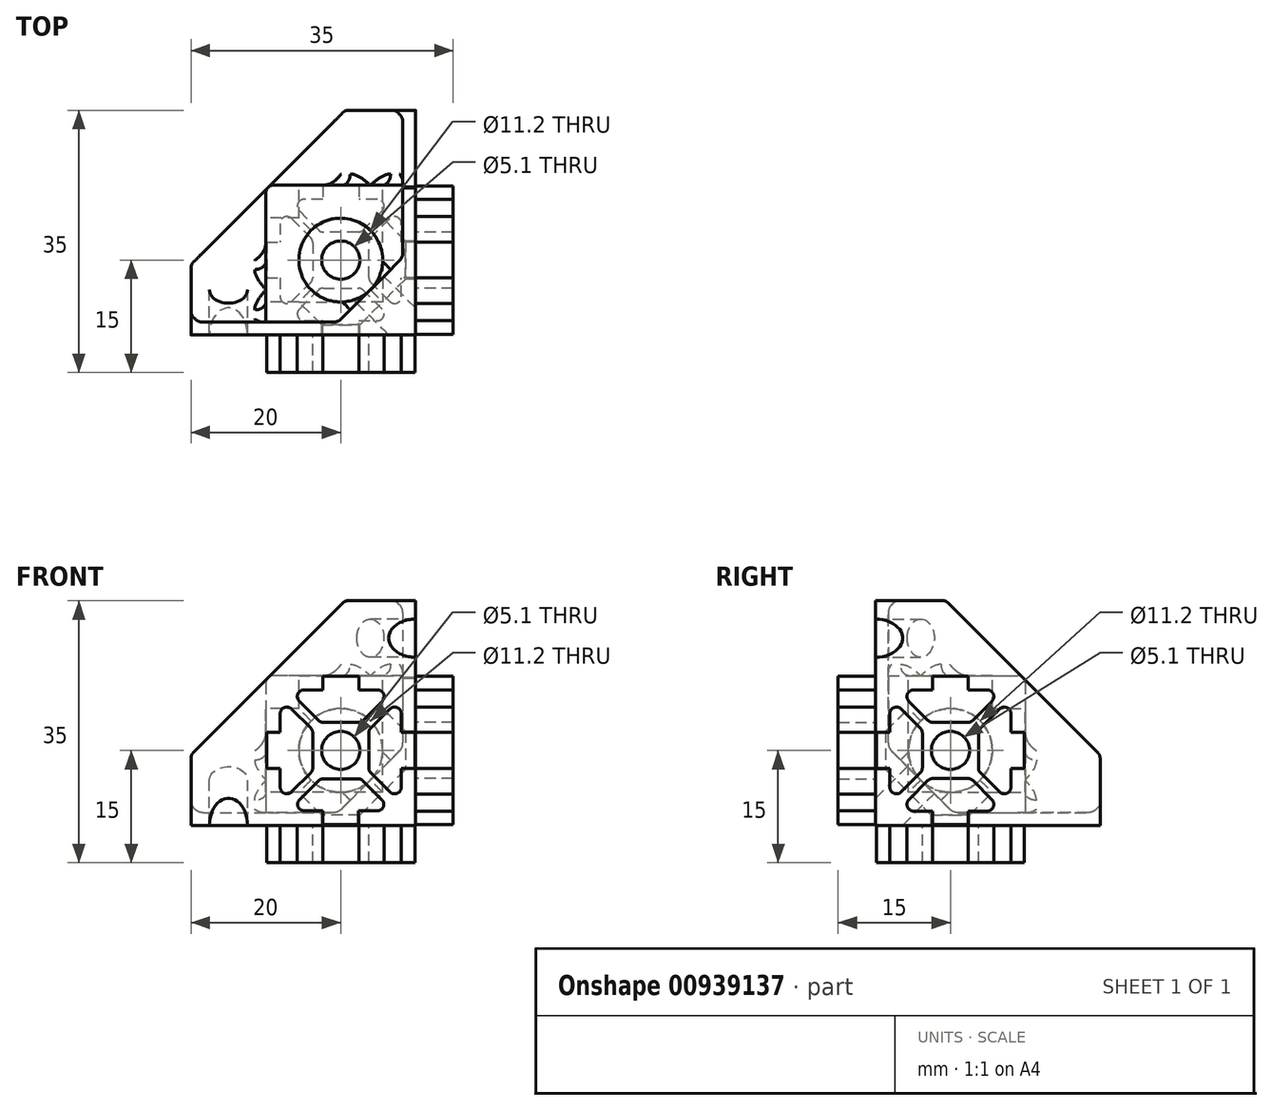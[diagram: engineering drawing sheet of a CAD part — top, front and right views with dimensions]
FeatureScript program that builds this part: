
annotation { "Feature Type Name" : "Feature", "Feature Type Description" : "" }
export const myFeature = defineFeature(function(context is Context, id is Id, definition is map)
    precondition{}
    {
        {
            var Q0;
            Q0=qCreatedBy(makeId("Top.planeOp"),FACE);
            var sketch = newSketch(context, id + "F0", { "sketchPlane" : qUnion([Q0]) });
            skLineSegment(sketch, "E0.bottom", {"start": v(0, 0) * mm, "end": v(-20, 0) * mm});
            skLineSegment(sketch, "E0.top", {"start": v(0, 20) * mm, "end": v(-20, 20) * mm});
            skLineSegment(sketch, "E0.left", {"start": v(0, 0) * mm, "end": v(0, 20) * mm});
            skLineSegment(sketch, "E0.right", {"start": v(-20, 0) * mm, "end": v(-20, 20) * mm});
            skSolve(sketch);
        }
        {
            var Q0;
            Q0 = qSketchRegion(id + "F0", true);
            extrude(context, id + "F1", {"entities" : qUnion([Q0]), "depth" : 20 * mm, "offsetDistance" : 25 * mm});
        }
        {
            var Q0;
            Q0=makeQuery(id+"FwfA9fW3TVrLifJ_1.boolean.opBoolean","SPLIT",EDGE,{"derivedFrom":makeQuery(id+"F1.opExtrude","CAP_EDGE",EDGE,{"disambiguationData":[OSD([sQuery(id+"F0.wireOp",EDGE,"E0.right")])],"isStart":false})});
            var Q1;
            Q1=makeQuery(id+"FhSoDMzTukZfK2q_1.boolean.opBoolean","SPLIT",EDGE,{"derivedFrom":makeQuery(id+"F1.opExtrude","SWEPT_EDGE",EDGE,{"disambiguationData":[OSD([sQuery(id+"F0.wireOp",EDGE,"E0.top"),sQuery(id+"F0.wireOp",EDGE,"E0.right")])]})});
            var Q2;
            Q2=makeQuery(id+"F1.opExtrude","CAP_EDGE",EDGE,{"disambiguationData":[OSD([sQuery(id+"F0.wireOp",EDGE,"E0.top")])],"isStart":false});
            fillet(context, id + "F2", {"entities" : qUnion([Q0, Q1, Q2]), "radius" : 1 * mm, "tangentPropagation" : true});
        }
        {
            var Q0;
            Q0=qCreatedBy(makeId("Front.planeOp"),FACE);
            cPlane(context, id + "F3", {"entities" : qUnion([Q0]), "cplaneType" : CPlaneType.OFFSET, "offset" : 10 * mm, "oppositeDirection" : true, "width" : 150 * mm, "height" : 150 * mm});
        }
        {
            var Q0;
            Q0=qCreatedBy(id+"F3.planeOp",FACE);
            var sketch = newSketch(context, id + "F4", { "sketchPlane" : qUnion([Q0]) });
            skLineSegment(sketch, "E1", {"start": v(0, 10) * mm, "end": v(-20, 10) * mm});
            skLineSegment(sketch, "E2", {"start": v(0, 7.45) * mm, "end": v(-1.35, 7.45) * mm});
            skLineSegment(sketch, "E3", {"start": v(-4.4, 4.4) * mm, "end": v(-20, 4.4) * mm});
            skLineSegment(sketch, "E4", {"start": v(-1.35, 7.45) * mm, "end": v(-4.4, 4.4) * mm});
            skLineSegment(sketch, "E5", {"start": v(-20, 10) * mm, "end": v(-20, 4.4) * mm});
            skLineSegment(sketch, "E6", {"start": v(0, 10) * mm, "end": v(0, 7.45) * mm});
            skSolve(sketch);
        }
        {
            var Q0;
            Q0 = qSketchRegion(id + "F4", true);
            var Q1;
            Q1=sQuery(id+"F4.wireOp",EDGE,"E1");
            revolve(context, id + "F5", {"operationType" : NewBodyOperationType.REMOVE, "surfaceOperationType" : NewSurfaceOperationType.NEW, "entities" : qUnion([Q0]), "axis" : qUnion([Q1]), "revolveType" : RevolveType.FULL, "oppositeDirection" : true});
        }
        {
            var Q0;
            Q0=qCreatedBy(id+"F3.planeOp",FACE);
            var sketch = newSketch(context, id + "F6", { "sketchPlane" : qUnion([Q0]) });
            skLineSegment(sketch, "E7", {"start": v(-15.6, 20) * mm, "end": v(-10, 20) * mm});
            skLineSegment(sketch, "E8", {"start": v(-10, 0) * mm, "end": v(-12.55, 0) * mm});
            skLineSegment(sketch, "E9", {"start": v(-10, 0) * mm, "end": v(-10, 20) * mm});
            skLineSegment(sketch, "E10", {"start": v(-12.55, 0) * mm, "end": v(-12.55, 1.35) * mm});
            skLineSegment(sketch, "E11", {"start": v(-15.6, 4.4) * mm, "end": v(-15.6, 20) * mm});
            skLineSegment(sketch, "E12", {"start": v(-12.55, 1.35) * mm, "end": v(-15.6, 4.4) * mm});
            skSolve(sketch);
        }
        {
            var Q0;
            Q0 = qSketchRegion(id + "F6", true);
            var Q1;
            Q1=sQuery(id+"F6.wireOp",EDGE,"E9");
            revolve(context, id + "F7", {"operationType" : NewBodyOperationType.REMOVE, "surfaceOperationType" : NewSurfaceOperationType.NEW, "entities" : qUnion([Q0]), "axis" : qUnion([Q1]), "revolveType" : RevolveType.FULL, "oppositeDirection" : true});
        }
        {
            var Q0;
            Q0=qCreatedBy(makeId("Right.planeOp"),FACE);
            cPlane(context, id + "F8", {"entities" : qUnion([Q0]), "cplaneType" : CPlaneType.OFFSET, "offset" : 10 * mm, "oppositeDirection" : true, "width" : 150 * mm, "height" : 150 * mm});
        }
        {
            var Q0;
            Q0=qCreatedBy(id+"F8.planeOp",FACE);
            var sketch = newSketch(context, id + "F9", { "sketchPlane" : qUnion([Q0]) });
            skLineSegment(sketch, "E13", {"start": v(20, 15.6) * mm, "end": v(20, 10) * mm});
            skLineSegment(sketch, "E14", {"start": v(0, 10) * mm, "end": v(0, 12.55) * mm});
            skLineSegment(sketch, "E15", {"start": v(0, 10) * mm, "end": v(20, 10) * mm});
            skLineSegment(sketch, "E16", {"start": v(0, 12.55) * mm, "end": v(1.35, 12.55) * mm});
            skLineSegment(sketch, "E17", {"start": v(4.4, 15.6) * mm, "end": v(20, 15.6) * mm});
            skLineSegment(sketch, "E18", {"start": v(1.35, 12.55) * mm, "end": v(4.4, 15.6) * mm});
            skSolve(sketch);
        }
        {
            var Q0;
            Q0 = qSketchRegion(id + "F9", true);
            var Q1;
            Q1=sQuery(id+"F9.wireOp",EDGE,"E15");
            revolve(context, id + "F10", {"operationType" : NewBodyOperationType.REMOVE, "surfaceOperationType" : NewSurfaceOperationType.NEW, "entities" : qUnion([Q0]), "axis" : qUnion([Q1]), "revolveType" : RevolveType.FULL, "oppositeDirection" : true});
        }
        {
            var Q0;
            Q0=makeQuery(id+"F1.opExtrude","SWEPT_FACE",FACE,{"disambiguationData":[OSD([sQuery(id+"F0.wireOp",EDGE,"E0.bottom")])]});
            var sketch = newSketch(context, id + "F11", { "sketchPlane" : qUnion([Q0]) });
            skLineSegment(sketch, "E19", {"start": v(-1.8, 12.5) * mm, "end": v(0, 12.5) * mm});
            skLineSegment(sketch, "E20", {"start": v(-20, 12.5) * mm, "end": v(-18.2, 12.5) * mm});
            skLineSegment(sketch, "E21", {"start": v(-1.8, 7.5) * mm, "end": v(0, 7.5) * mm});
            skLineSegment(sketch, "E22", {"start": v(-20, 7.5) * mm, "end": v(-18.2, 7.5) * mm});
            skLineSegment(sketch, "E23", {"start": v(-12.5, 1.8) * mm, "end": v(-12.5, 0) * mm});
            skLineSegment(sketch, "E24", {"start": v(-12.5, 20) * mm, "end": v(-12.5, 18.2) * mm});
            skLineSegment(sketch, "E25", {"start": v(-7.54, 1.76) * mm, "end": v(-7.54, 0) * mm});
            skLineSegment(sketch, "E26", {"start": v(-7.5, 20) * mm, "end": v(-7.5, 18.2) * mm});
            skLineSegment(sketch, "E27", {"start": v(-7.5, 1.84) * mm, "end": v(-5.1, 1.84) * mm});
            skLineSegment(sketch, "E28", {"start": v(-1.8, 5.1) * mm, "end": v(-1.8, 7.5) * mm});
            skLineSegment(sketch, "E29", {"start": v(-1.8, 12.5) * mm, "end": v(-1.8, 14.9) * mm});
            skLineSegment(sketch, "E30", {"start": v(-7.5, 18.2) * mm, "end": v(-5.1, 18.2) * mm});
            skLineSegment(sketch, "E31", {"start": v(-14.9, 18.2) * mm, "end": v(-12.5, 18.2) * mm});
            skLineSegment(sketch, "E32", {"start": v(-18.2, 14.9) * mm, "end": v(-18.2, 12.5) * mm});
            skLineSegment(sketch, "E33", {"start": v(-18.2, 7.5) * mm, "end": v(-18.2, 5.1) * mm});
            skLineSegment(sketch, "E34", {"start": v(-14.9, 1.84) * mm, "end": v(-12.5, 1.84) * mm});
            skLineSegment(sketch, "E35", {"start": v(-6.06, 6.94) * mm, "end": v(-3.5, 4.4) * mm});
            skLineSegment(sketch, "E36", {"start": v(-15.6, 16.5) * mm, "end": v(-13.06, 13.94) * mm});
            skLineSegment(sketch, "E37", {"start": v(-6.97, 6.03) * mm, "end": v(-4.42, 3.48) * mm});
            skLineSegment(sketch, "E38", {"start": v(-16.5, 15.6) * mm, "end": v(-13.94, 13.06) * mm});
            skLineSegment(sketch, "E39", {"start": v(-13.94, 6.94) * mm, "end": v(-16.5, 4.4) * mm});
            skLineSegment(sketch, "E40", {"start": v(-4.4, 16.5) * mm, "end": v(-6.94, 13.94) * mm});
            skLineSegment(sketch, "E41", {"start": v(-6.06, 13.06) * mm, "end": v(-3.5, 15.6) * mm});
            skLineSegment(sketch, "E42", {"start": v(-15.58, 3.48) * mm, "end": v(-13.03, 6.03) * mm});
            skLineSegment(sketch, "E43", {"start": v(-13.65, 12.35) * mm, "end": v(-13.65, 7.65) * mm});
            skLineSegment(sketch, "E44", {"start": v(-6.35, 7.65) * mm, "end": v(-6.35, 12.35) * mm});
            skArc(sketch, "E45", {"start": v(-6.35, 7.65) * mm, "mid": v(-6.27, 7.27) * mm, "end": v(-6.06, 6.94) * mm});
            skArc(sketch, "E46", {"start": v(-6.06, 13.06) * mm, "mid": v(-6.27, 12.73) * mm, "end": v(-6.35, 12.35) * mm});
            skArc(sketch, "E47", {"start": v(-13.94, 6.94) * mm, "mid": v(-13.73, 7.27) * mm, "end": v(-13.65, 7.65) * mm});
            skArc(sketch, "E48", {"start": v(-13.65, 12.35) * mm, "mid": v(-13.73, 12.73) * mm, "end": v(-13.94, 13.06) * mm});
            skLineSegment(sketch, "E49", {"start": v(-12.35, 13.65) * mm, "end": v(-7.65, 13.65) * mm});
            skLineSegment(sketch, "E50", {"start": v(-12.35, 6.31) * mm, "end": v(-7.65, 6.31) * mm});
            skArc(sketch, "E51", {"start": v(-6.97, 6.03) * mm, "mid": v(-7.28, 6.24) * mm, "end": v(-7.65, 6.31) * mm});
            skArc(sketch, "E52", {"start": v(-7.65, 13.65) * mm, "mid": v(-7.27, 13.73) * mm, "end": v(-6.94, 13.94) * mm});
            skArc(sketch, "E53", {"start": v(-12.35, 6.31) * mm, "mid": v(-12.72, 6.24) * mm, "end": v(-13.03, 6.03) * mm});
            skArc(sketch, "E54", {"start": v(-13.06, 13.94) * mm, "mid": v(-12.73, 13.73) * mm, "end": v(-12.35, 13.65) * mm});
            skArc(sketch, "E55", {"start": v(-16.5, 15.6) * mm, "mid": v(-17.58, 15.82) * mm, "end": v(-18.2, 14.9) * mm});
            skArc(sketch, "E56", {"start": v(-14.9, 18.2) * mm, "mid": v(-15.82, 17.58) * mm, "end": v(-15.6, 16.5) * mm});
            skArc(sketch, "E57", {"start": v(-4.4, 16.5) * mm, "mid": v(-4.18, 17.58) * mm, "end": v(-5.1, 18.2) * mm});
            skArc(sketch, "E58", {"start": v(-1.8, 14.9) * mm, "mid": v(-2.42, 15.82) * mm, "end": v(-3.5, 15.6) * mm});
            skArc(sketch, "E59", {"start": v(-3.5, 4.4) * mm, "mid": v(-2.42, 4.18) * mm, "end": v(-1.8, 5.1) * mm});
            skArc(sketch, "E60", {"start": v(-5.1, 1.84) * mm, "mid": v(-4.21, 2.43) * mm, "end": v(-4.42, 3.48) * mm});
            skArc(sketch, "E61", {"start": v(-15.58, 3.48) * mm, "mid": v(-15.79, 2.43) * mm, "end": v(-14.9, 1.84) * mm});
            skArc(sketch, "E62", {"start": v(-18.2, 5.1) * mm, "mid": v(-17.58, 4.18) * mm, "end": v(-16.5, 4.4) * mm});
            skLineSegment(sketch, "E63", {"start": v(-12.5, 20) * mm, "end": v(-7.5, 20) * mm});
            skLineSegment(sketch, "E64", {"start": v(-20, 12.5) * mm, "end": v(-20, 7.5) * mm});
            skLineSegment(sketch, "E65", {"start": v(-12.5, 0) * mm, "end": v(-7.54, 0) * mm});
            skLineSegment(sketch, "E66", {"start": v(0, 12.5) * mm, "end": v(0, 7.5) * mm});
            skLineSegment(sketch, "E67.0", {"start": v(-12.4, 19.9) * mm, "end": v(-7.6, 19.9) * mm});
            skArc(sketch, "E67.1", {"start": v(-12.99, 14.01) * mm, "mid": v(-12.7, 13.82) * mm, "end": v(-12.35, 13.75) * mm});
            skLineSegment(sketch, "E67.2", {"start": v(-15.54, 16.56) * mm, "end": v(-12.99, 14.01) * mm});
            skArc(sketch, "E67.3", {"start": v(-14.9, 18.1) * mm, "mid": v(-15.73, 17.54) * mm, "end": v(-15.54, 16.56) * mm});
            skLineSegment(sketch, "E67.4", {"start": v(-14.9, 18.1) * mm, "end": v(-12.4, 18.1) * mm});
            skLineSegment(sketch, "E67.5", {"start": v(-12.35, 13.75) * mm, "end": v(-7.65, 13.75) * mm});
            skLineSegment(sketch, "E67.6", {"start": v(-12.4, 19.9) * mm, "end": v(-12.4, 18.1) * mm});
            skArc(sketch, "E67.7", {"start": v(-7.65, 13.75) * mm, "mid": v(-7.3, 13.82) * mm, "end": v(-7.01, 14.01) * mm});
            skLineSegment(sketch, "E67.8", {"start": v(-4.46, 16.56) * mm, "end": v(-7.01, 14.01) * mm});
            skArc(sketch, "E67.9", {"start": v(-4.46, 16.56) * mm, "mid": v(-4.27, 17.54) * mm, "end": v(-5.1, 18.1) * mm});
            skLineSegment(sketch, "E67.10", {"start": v(-7.6, 18.1) * mm, "end": v(-5.1, 18.1) * mm});
            skLineSegment(sketch, "E67.11", {"start": v(-7.6, 19.9) * mm, "end": v(-7.6, 18.1) * mm});
            skArc(sketch, "E68.0", {"start": v(-13.75, 12.35) * mm, "mid": v(-13.82, 12.7) * mm, "end": v(-14.01, 12.99) * mm});
            skLineSegment(sketch, "E68.1", {"start": v(-18.1, 7.6) * mm, "end": v(-18.1, 5.1) * mm});
            skArc(sketch, "E68.2", {"start": v(-18.1, 5.1) * mm, "mid": v(-17.54, 4.27) * mm, "end": v(-16.56, 4.46) * mm});
            skLineSegment(sketch, "E68.3", {"start": v(-14.01, 7.01) * mm, "end": v(-16.56, 4.46) * mm});
            skArc(sketch, "E68.4", {"start": v(-14.01, 7.01) * mm, "mid": v(-13.82, 7.3) * mm, "end": v(-13.75, 7.65) * mm});
            skLineSegment(sketch, "E68.5", {"start": v(-19.9, 7.6) * mm, "end": v(-18.1, 7.6) * mm});
            skLineSegment(sketch, "E68.6", {"start": v(-13.75, 12.35) * mm, "end": v(-13.75, 7.65) * mm});
            skLineSegment(sketch, "E68.7", {"start": v(-19.9, 12.4) * mm, "end": v(-19.9, 7.6) * mm});
            skLineSegment(sketch, "E68.8", {"start": v(-19.9, 12.4) * mm, "end": v(-18.1, 12.4) * mm});
            skLineSegment(sketch, "E68.9", {"start": v(-18.1, 14.9) * mm, "end": v(-18.1, 12.4) * mm});
            skArc(sketch, "E68.10", {"start": v(-16.56, 15.54) * mm, "mid": v(-17.54, 15.73) * mm, "end": v(-18.1, 14.9) * mm});
            skLineSegment(sketch, "E68.11", {"start": v(-16.56, 15.54) * mm, "end": v(-14.01, 12.99) * mm});
            skArc(sketch, "E69.0", {"start": v(-12.35, 6.21) * mm, "mid": v(-12.68, 6.14) * mm, "end": v(-12.96, 5.96) * mm});
            skLineSegment(sketch, "E69.1", {"start": v(-7.64, 1.94) * mm, "end": v(-5.1, 1.94) * mm});
            skArc(sketch, "E69.2", {"start": v(-5.1, 1.94) * mm, "mid": v(-4.3, 2.47) * mm, "end": v(-4.5, 3.4) * mm});
            skLineSegment(sketch, "E69.3", {"start": v(-7.04, 5.96) * mm, "end": v(-4.5, 3.4) * mm});
            skArc(sketch, "E69.4", {"start": v(-7.04, 5.96) * mm, "mid": v(-7.32, 6.14) * mm, "end": v(-7.65, 6.21) * mm});
            skLineSegment(sketch, "E69.5", {"start": v(-7.64, 1.94) * mm, "end": v(-7.64, 0.1) * mm});
            skLineSegment(sketch, "E69.6", {"start": v(-12.35, 6.21) * mm, "end": v(-7.65, 6.21) * mm});
            skLineSegment(sketch, "E69.7", {"start": v(-12.4, 0.1) * mm, "end": v(-7.64, 0.1) * mm});
            skLineSegment(sketch, "E69.8", {"start": v(-12.4, 1.94) * mm, "end": v(-12.4, 0.1) * mm});
            skLineSegment(sketch, "E69.9", {"start": v(-14.9, 1.94) * mm, "end": v(-12.4, 1.94) * mm});
            skArc(sketch, "E69.10", {"start": v(-15.5, 3.4) * mm, "mid": v(-15.7, 2.47) * mm, "end": v(-14.9, 1.94) * mm});
            skLineSegment(sketch, "E69.11", {"start": v(-15.5, 3.4) * mm, "end": v(-12.96, 5.96) * mm});
            skArc(sketch, "E70.0", {"start": v(-6.25, 7.65) * mm, "mid": v(-6.18, 7.3) * mm, "end": v(-5.99, 7.01) * mm});
            skLineSegment(sketch, "E70.1", {"start": v(-1.9, 12.4) * mm, "end": v(-1.9, 14.9) * mm});
            skArc(sketch, "E70.2", {"start": v(-1.9, 14.9) * mm, "mid": v(-2.46, 15.73) * mm, "end": v(-3.44, 15.54) * mm});
            skLineSegment(sketch, "E70.3", {"start": v(-5.99, 12.99) * mm, "end": v(-3.44, 15.54) * mm});
            skArc(sketch, "E70.4", {"start": v(-5.99, 12.99) * mm, "mid": v(-6.18, 12.7) * mm, "end": v(-6.25, 12.35) * mm});
            skLineSegment(sketch, "E70.5", {"start": v(-1.9, 12.4) * mm, "end": v(-0.1, 12.4) * mm});
            skLineSegment(sketch, "E70.6", {"start": v(-6.25, 7.65) * mm, "end": v(-6.25, 12.35) * mm});
            skLineSegment(sketch, "E70.7", {"start": v(-0.1, 12.4) * mm, "end": v(-0.1, 7.6) * mm});
            skLineSegment(sketch, "E70.8", {"start": v(-1.9, 7.6) * mm, "end": v(-0.1, 7.6) * mm});
            skLineSegment(sketch, "E70.9", {"start": v(-1.9, 5.1) * mm, "end": v(-1.9, 7.6) * mm});
            skArc(sketch, "E70.10", {"start": v(-3.44, 4.46) * mm, "mid": v(-2.46, 4.27) * mm, "end": v(-1.9, 5.1) * mm});
            skLineSegment(sketch, "E70.11", {"start": v(-5.99, 7.01) * mm, "end": v(-3.44, 4.46) * mm});
            skSolve(sketch);
        }
        {
            var Q0;
            Q0=makeQuery(id+"F11.imprint","IMPRINT",FACE,{"disambiguationData":[TD([[makeQuery(id+"F11.imprint","IMPRINT",EDGE,{"derivedFrom":sQuery(id+"F11.wireOp",EDGE,"E67.0")}),-1.0]])]});
            var Q1;
            Q1=makeQuery(id+"F11.imprint","IMPRINT",FACE,{"disambiguationData":[TD([[makeQuery(id+"F11.imprint","IMPRINT",EDGE,{"derivedFrom":sQuery(id+"F11.wireOp",EDGE,"E68.0")}),1.0]])]});
            var Q2;
            Q2=makeQuery(id+"F11.imprint","IMPRINT",FACE,{"disambiguationData":[TD([[makeQuery(id+"F11.imprint","IMPRINT",EDGE,{"derivedFrom":sQuery(id+"F11.wireOp",EDGE,"E70.0")}),1.0]])]});
            var Q3;
            Q3=makeQuery(id+"F11.imprint","IMPRINT",FACE,{"disambiguationData":[TD([[makeQuery(id+"F11.imprint","IMPRINT",EDGE,{"derivedFrom":sQuery(id+"F11.wireOp",EDGE,"E69.0")}),1.0]])]});
            extrude(context, id + "F12", {"entities" : qUnion([Q0, Q1, Q2, Q3]), "operationType" : NewBodyOperationType.ADD, "depth" : 5 * mm, "offsetDistance" : 25 * mm});
        }
        {
            var Q0;
            Q0=makeQuery(id+"F1.opExtrude","SWEPT_FACE",FACE,{"disambiguationData":[OSD([sQuery(id+"F0.wireOp",EDGE,"E0.left")])]});
            var sketch = newSketch(context, id + "F13", { "sketchPlane" : qUnion([Q0]) });
            skLineSegment(sketch, "E71", {"start": v(7.5, 20) * mm, "end": v(7.5, 18.2) * mm});
            skLineSegment(sketch, "E72", {"start": v(12.5, 20) * mm, "end": v(12.5, 18.2) * mm});
            skLineSegment(sketch, "E73", {"start": v(12.5, 18.2) * mm, "end": v(14.9, 18.2) * mm});
            skLineSegment(sketch, "E74", {"start": v(5.1, 18.2) * mm, "end": v(7.5, 18.2) * mm});
            skLineSegment(sketch, "E75", {"start": v(4.4, 16.5) * mm, "end": v(6.94, 13.94) * mm});
            skLineSegment(sketch, "E76", {"start": v(15.6, 16.5) * mm, "end": v(13.06, 13.94) * mm});
            skLineSegment(sketch, "E77", {"start": v(7.65, 13.65) * mm, "end": v(12.35, 13.65) * mm});
            skArc(sketch, "E78", {"start": v(12.35, 13.65) * mm, "mid": v(12.73, 13.73) * mm, "end": v(13.06, 13.94) * mm});
            skArc(sketch, "E79", {"start": v(6.94, 13.94) * mm, "mid": v(7.27, 13.73) * mm, "end": v(7.65, 13.65) * mm});
            skArc(sketch, "E80", {"start": v(5.1, 18.2) * mm, "mid": v(4.18, 17.58) * mm, "end": v(4.4, 16.5) * mm});
            skArc(sketch, "E81", {"start": v(15.6, 16.5) * mm, "mid": v(15.82, 17.58) * mm, "end": v(14.9, 18.2) * mm});
            skLineSegment(sketch, "E82", {"start": v(7.5, 20) * mm, "end": v(12.5, 20) * mm});
            skPoint(sketch, "E83", {"position": v(10, 10) * mm});
            skArc(sketch, "E84.0", {"start": v(7.01, 14.01) * mm, "mid": v(7.3, 13.82) * mm, "end": v(7.65, 13.75) * mm});
            skLineSegment(sketch, "E84.1", {"start": v(12.4, 18.1) * mm, "end": v(14.9, 18.1) * mm});
            skArc(sketch, "E84.2", {"start": v(15.54, 16.56) * mm, "mid": v(15.73, 17.54) * mm, "end": v(14.9, 18.1) * mm});
            skLineSegment(sketch, "E84.3", {"start": v(15.54, 16.56) * mm, "end": v(12.99, 14.01) * mm});
            skArc(sketch, "E84.4", {"start": v(12.35, 13.75) * mm, "mid": v(12.7, 13.82) * mm, "end": v(12.99, 14.01) * mm});
            skLineSegment(sketch, "E84.5", {"start": v(12.4, 19.9) * mm, "end": v(12.4, 18.1) * mm});
            skLineSegment(sketch, "E84.6", {"start": v(7.65, 13.75) * mm, "end": v(12.35, 13.75) * mm});
            skLineSegment(sketch, "E84.7", {"start": v(7.6, 19.9) * mm, "end": v(12.4, 19.9) * mm});
            skLineSegment(sketch, "E84.8", {"start": v(7.6, 19.9) * mm, "end": v(7.6, 18.1) * mm});
            skLineSegment(sketch, "E84.9", {"start": v(5.1, 18.1) * mm, "end": v(7.6, 18.1) * mm});
            skArc(sketch, "E84.10", {"start": v(5.1, 18.1) * mm, "mid": v(4.27, 17.54) * mm, "end": v(4.46, 16.56) * mm});
            skLineSegment(sketch, "E84.11", {"start": v(4.46, 16.56) * mm, "end": v(7.01, 14.01) * mm});
            skLineSegment(sketch, "E85.1.0", {"start": v(0.1, 7.6) * mm, "end": v(1.9, 7.6) * mm});
            skLineSegment(sketch, "E85.1.1", {"start": v(1.9, 5.1) * mm, "end": v(1.9, 7.6) * mm});
            skArc(sketch, "E85.1.2", {"start": v(1.9, 5.1) * mm, "mid": v(2.46, 4.27) * mm, "end": v(3.44, 4.46) * mm});
            skLineSegment(sketch, "E85.1.3", {"start": v(3.44, 4.46) * mm, "end": v(5.99, 7.01) * mm});
            skArc(sketch, "E85.1.4", {"start": v(5.99, 7.01) * mm, "mid": v(6.18, 7.3) * mm, "end": v(6.25, 7.65) * mm});
            skLineSegment(sketch, "E85.1.5", {"start": v(6.25, 7.65) * mm, "end": v(6.25, 12.35) * mm});
            skArc(sketch, "E85.1.6", {"start": v(6.25, 12.35) * mm, "mid": v(6.18, 12.7) * mm, "end": v(5.99, 12.99) * mm});
            skLineSegment(sketch, "E85.1.7", {"start": v(3.44, 15.54) * mm, "end": v(5.99, 12.99) * mm});
            skArc(sketch, "E85.1.8", {"start": v(3.44, 15.54) * mm, "mid": v(2.46, 15.73) * mm, "end": v(1.9, 14.9) * mm});
            skLineSegment(sketch, "E85.1.9", {"start": v(1.9, 12.4) * mm, "end": v(1.9, 14.9) * mm});
            skLineSegment(sketch, "E85.1.10", {"start": v(0.1, 12.4) * mm, "end": v(1.9, 12.4) * mm});
            skLineSegment(sketch, "E85.1.11", {"start": v(0.1, 7.6) * mm, "end": v(0.1, 12.4) * mm});
            skLineSegment(sketch, "E85.2.0", {"start": v(12.4, 0.1) * mm, "end": v(12.4, 1.9) * mm});
            skLineSegment(sketch, "E85.2.1", {"start": v(14.9, 1.9) * mm, "end": v(12.4, 1.9) * mm});
            skArc(sketch, "E85.2.2", {"start": v(14.9, 1.9) * mm, "mid": v(15.73, 2.46) * mm, "end": v(15.54, 3.44) * mm});
            skLineSegment(sketch, "E85.2.3", {"start": v(15.54, 3.44) * mm, "end": v(12.99, 5.99) * mm});
            skArc(sketch, "E85.2.4", {"start": v(12.99, 5.99) * mm, "mid": v(12.7, 6.18) * mm, "end": v(12.35, 6.25) * mm});
            skLineSegment(sketch, "E85.2.5", {"start": v(12.35, 6.25) * mm, "end": v(7.65, 6.25) * mm});
            skArc(sketch, "E85.2.6", {"start": v(7.65, 6.25) * mm, "mid": v(7.3, 6.18) * mm, "end": v(7.01, 5.99) * mm});
            skLineSegment(sketch, "E85.2.7", {"start": v(4.46, 3.44) * mm, "end": v(7.01, 5.99) * mm});
            skArc(sketch, "E85.2.8", {"start": v(4.46, 3.44) * mm, "mid": v(4.27, 2.46) * mm, "end": v(5.1, 1.9) * mm});
            skLineSegment(sketch, "E85.2.9", {"start": v(7.6, 1.9) * mm, "end": v(5.1, 1.9) * mm});
            skLineSegment(sketch, "E85.2.10", {"start": v(7.6, 0.1) * mm, "end": v(7.6, 1.9) * mm});
            skLineSegment(sketch, "E85.2.11", {"start": v(12.4, 0.1) * mm, "end": v(7.6, 0.1) * mm});
            skLineSegment(sketch, "E85.3.0", {"start": v(19.9, 12.4) * mm, "end": v(18.1, 12.4) * mm});
            skLineSegment(sketch, "E85.3.1", {"start": v(18.1, 14.9) * mm, "end": v(18.1, 12.4) * mm});
            skArc(sketch, "E85.3.2", {"start": v(18.1, 14.9) * mm, "mid": v(17.54, 15.73) * mm, "end": v(16.56, 15.54) * mm});
            skLineSegment(sketch, "E85.3.3", {"start": v(16.56, 15.54) * mm, "end": v(14.01, 12.99) * mm});
            skArc(sketch, "E85.3.4", {"start": v(14.01, 12.99) * mm, "mid": v(13.82, 12.7) * mm, "end": v(13.75, 12.35) * mm});
            skLineSegment(sketch, "E85.3.5", {"start": v(13.75, 12.35) * mm, "end": v(13.75, 7.65) * mm});
            skArc(sketch, "E85.3.6", {"start": v(13.75, 7.65) * mm, "mid": v(13.82, 7.3) * mm, "end": v(14.01, 7.01) * mm});
            skLineSegment(sketch, "E85.3.7", {"start": v(16.56, 4.46) * mm, "end": v(14.01, 7.01) * mm});
            skArc(sketch, "E85.3.8", {"start": v(16.56, 4.46) * mm, "mid": v(17.54, 4.27) * mm, "end": v(18.1, 5.1) * mm});
            skLineSegment(sketch, "E85.3.9", {"start": v(18.1, 7.6) * mm, "end": v(18.1, 5.1) * mm});
            skLineSegment(sketch, "E85.3.10", {"start": v(19.9, 7.6) * mm, "end": v(18.1, 7.6) * mm});
            skLineSegment(sketch, "E85.3.11", {"start": v(19.9, 12.4) * mm, "end": v(19.9, 7.6) * mm});
            skSolve(sketch);
        }
        {
            var Q0;
            Q0=makeQuery(id+"F13.imprint","IMPRINT",FACE,{"disambiguationData":[TD([[makeQuery(id+"F13.imprint","IMPRINT",EDGE,{"derivedFrom":sQuery(id+"F13.wireOp",EDGE,"E84.0")}),1.0]])]});
            var Q1;
            Q1=makeQuery(id+"F13.imprint","IMPRINT",FACE,{"disambiguationData":[TD([[makeQuery(id+"F13.imprint","IMPRINT",EDGE,{"derivedFrom":sQuery(id+"F13.wireOp",EDGE,"E85.3.0")}),1.0]])]});
            var Q2;
            Q2=makeQuery(id+"F13.imprint","IMPRINT",FACE,{"disambiguationData":[TD([[makeQuery(id+"F13.imprint","IMPRINT",EDGE,{"derivedFrom":sQuery(id+"F13.wireOp",EDGE,"E85.2.0")}),1.0]])]});
            var Q3;
            Q3=makeQuery(id+"F13.imprint","IMPRINT",FACE,{"disambiguationData":[TD([[makeQuery(id+"F13.imprint","IMPRINT",EDGE,{"derivedFrom":sQuery(id+"F13.wireOp",EDGE,"E85.1.0")}),1.0]])]});
            extrude(context, id + "F14", {"entities" : qUnion([Q0, Q1, Q2, Q3]), "operationType" : NewBodyOperationType.ADD, "depth" : 5 * mm, "offsetDistance" : 25 * mm});
        }
        {
            var Q0;
            Q0=makeQuery(id+"F1.opExtrude","CAP_FACE",FACE,{"disambiguationData":[OSD([sQuery(id+"F0.wireOp",EDGE,"E0.bottom"),sQuery(id+"F0.wireOp",EDGE,"E0.top"),sQuery(id+"F0.wireOp",EDGE,"E0.left"),sQuery(id+"F0.wireOp",EDGE,"E0.right")])],"isStart":true});
            var sketch = newSketch(context, id + "F15", { "sketchPlane" : qUnion([Q0]) });
            skLineSegment(sketch, "E86", {"start": v(-12.5, 0) * mm, "end": v(-12.5, -1.8) * mm});
            skLineSegment(sketch, "E87", {"start": v(-7.5, 0) * mm, "end": v(-7.5, -1.8) * mm});
            skLineSegment(sketch, "E88", {"start": v(-7.5, -1.8) * mm, "end": v(-5.1, -1.8) * mm});
            skLineSegment(sketch, "E89", {"start": v(-14.9, -1.8) * mm, "end": v(-12.5, -1.8) * mm});
            skLineSegment(sketch, "E90", {"start": v(-15.6, -3.5) * mm, "end": v(-13.06, -6.06) * mm});
            skLineSegment(sketch, "E91", {"start": v(-4.4, -3.5) * mm, "end": v(-6.94, -6.06) * mm});
            skLineSegment(sketch, "E92", {"start": v(-12.35, -6.35) * mm, "end": v(-7.65, -6.35) * mm});
            skArc(sketch, "E93", {"start": v(-7.65, -6.35) * mm, "mid": v(-7.27, -6.27) * mm, "end": v(-6.94, -6.06) * mm});
            skArc(sketch, "E94", {"start": v(-13.06, -6.06) * mm, "mid": v(-12.73, -6.27) * mm, "end": v(-12.35, -6.35) * mm});
            skArc(sketch, "E95", {"start": v(-14.9, -1.8) * mm, "mid": v(-15.82, -2.42) * mm, "end": v(-15.6, -3.5) * mm});
            skArc(sketch, "E96", {"start": v(-4.4, -3.5) * mm, "mid": v(-4.18, -2.42) * mm, "end": v(-5.1, -1.8) * mm});
            skLineSegment(sketch, "E97", {"start": v(-12.5, 0) * mm, "end": v(-7.5, 0) * mm});
            skArc(sketch, "E98.0", {"start": v(-12.99, -5.99) * mm, "mid": v(-12.7, -6.18) * mm, "end": v(-12.35, -6.25) * mm});
            skLineSegment(sketch, "E98.1", {"start": v(-7.6, -1.9) * mm, "end": v(-5.1, -1.9) * mm});
            skArc(sketch, "E98.2", {"start": v(-4.46, -3.44) * mm, "mid": v(-4.27, -2.46) * mm, "end": v(-5.1, -1.9) * mm});
            skLineSegment(sketch, "E98.3", {"start": v(-4.46, -3.44) * mm, "end": v(-7.01, -5.99) * mm});
            skArc(sketch, "E98.4", {"start": v(-7.65, -6.25) * mm, "mid": v(-7.3, -6.18) * mm, "end": v(-7.01, -5.99) * mm});
            skLineSegment(sketch, "E98.5", {"start": v(-7.6, -0.1) * mm, "end": v(-7.6, -1.9) * mm});
            skLineSegment(sketch, "E98.6", {"start": v(-12.35, -6.25) * mm, "end": v(-7.65, -6.25) * mm});
            skLineSegment(sketch, "E98.7", {"start": v(-12.4, -0.1) * mm, "end": v(-7.6, -0.1) * mm});
            skLineSegment(sketch, "E98.8", {"start": v(-12.4, -0.1) * mm, "end": v(-12.4, -1.9) * mm});
            skLineSegment(sketch, "E98.9", {"start": v(-14.9, -1.9) * mm, "end": v(-12.4, -1.9) * mm});
            skArc(sketch, "E98.10", {"start": v(-14.9, -1.9) * mm, "mid": v(-15.73, -2.46) * mm, "end": v(-15.54, -3.44) * mm});
            skLineSegment(sketch, "E98.11", {"start": v(-15.54, -3.44) * mm, "end": v(-12.99, -5.99) * mm});
            skLineSegment(sketch, "E99.1.0", {"start": v(-18.1, -14.9) * mm, "end": v(-18.1, -12.4) * mm});
            skArc(sketch, "E99.1.1", {"start": v(-18.1, -14.9) * mm, "mid": v(-17.54, -15.73) * mm, "end": v(-16.56, -15.54) * mm});
            skLineSegment(sketch, "E99.1.2", {"start": v(-16.56, -15.54) * mm, "end": v(-14.01, -12.99) * mm});
            skArc(sketch, "E99.1.3", {"start": v(-14.01, -12.99) * mm, "mid": v(-13.82, -12.7) * mm, "end": v(-13.75, -12.35) * mm});
            skLineSegment(sketch, "E99.1.4", {"start": v(-13.75, -12.35) * mm, "end": v(-13.75, -7.65) * mm});
            skArc(sketch, "E99.1.5", {"start": v(-13.75, -7.65) * mm, "mid": v(-13.82, -7.3) * mm, "end": v(-14.01, -7.01) * mm});
            skLineSegment(sketch, "E99.1.6", {"start": v(-16.56, -4.46) * mm, "end": v(-14.01, -7.01) * mm});
            skArc(sketch, "E99.1.7", {"start": v(-16.56, -4.46) * mm, "mid": v(-17.54, -4.27) * mm, "end": v(-18.1, -5.1) * mm});
            skLineSegment(sketch, "E99.1.8", {"start": v(-18.1, -7.6) * mm, "end": v(-18.1, -5.1) * mm});
            skLineSegment(sketch, "E99.1.9", {"start": v(-19.9, -7.6) * mm, "end": v(-18.1, -7.6) * mm});
            skLineSegment(sketch, "E99.1.10", {"start": v(-19.9, -12.4) * mm, "end": v(-19.9, -7.6) * mm});
            skLineSegment(sketch, "E99.1.11", {"start": v(-19.9, -12.4) * mm, "end": v(-18.1, -12.4) * mm});
            skLineSegment(sketch, "E99.2.0", {"start": v(-5.1, -18.1) * mm, "end": v(-7.6, -18.1) * mm});
            skArc(sketch, "E99.2.1", {"start": v(-5.1, -18.1) * mm, "mid": v(-4.27, -17.54) * mm, "end": v(-4.46, -16.56) * mm});
            skLineSegment(sketch, "E99.2.2", {"start": v(-4.46, -16.56) * mm, "end": v(-7.01, -14.01) * mm});
            skArc(sketch, "E99.2.3", {"start": v(-7.01, -14.01) * mm, "mid": v(-7.3, -13.82) * mm, "end": v(-7.65, -13.75) * mm});
            skLineSegment(sketch, "E99.2.4", {"start": v(-7.65, -13.75) * mm, "end": v(-12.35, -13.75) * mm});
            skArc(sketch, "E99.2.5", {"start": v(-12.35, -13.75) * mm, "mid": v(-12.7, -13.82) * mm, "end": v(-12.99, -14.01) * mm});
            skLineSegment(sketch, "E99.2.6", {"start": v(-15.54, -16.56) * mm, "end": v(-12.99, -14.01) * mm});
            skArc(sketch, "E99.2.7", {"start": v(-15.54, -16.56) * mm, "mid": v(-15.73, -17.54) * mm, "end": v(-14.9, -18.1) * mm});
            skLineSegment(sketch, "E99.2.8", {"start": v(-12.4, -18.1) * mm, "end": v(-14.9, -18.1) * mm});
            skLineSegment(sketch, "E99.2.9", {"start": v(-12.4, -19.9) * mm, "end": v(-12.4, -18.1) * mm});
            skLineSegment(sketch, "E99.2.10", {"start": v(-7.6, -19.9) * mm, "end": v(-12.4, -19.9) * mm});
            skLineSegment(sketch, "E99.2.11", {"start": v(-7.6, -19.9) * mm, "end": v(-7.6, -18.1) * mm});
            skLineSegment(sketch, "E99.3.0", {"start": v(-1.9, -5.1) * mm, "end": v(-1.9, -7.6) * mm});
            skArc(sketch, "E99.3.1", {"start": v(-1.9, -5.1) * mm, "mid": v(-2.46, -4.27) * mm, "end": v(-3.44, -4.46) * mm});
            skLineSegment(sketch, "E99.3.2", {"start": v(-3.44, -4.46) * mm, "end": v(-5.99, -7.01) * mm});
            skArc(sketch, "E99.3.3", {"start": v(-5.99, -7.01) * mm, "mid": v(-6.18, -7.3) * mm, "end": v(-6.25, -7.65) * mm});
            skLineSegment(sketch, "E99.3.4", {"start": v(-6.25, -7.65) * mm, "end": v(-6.25, -12.35) * mm});
            skArc(sketch, "E99.3.5", {"start": v(-6.25, -12.35) * mm, "mid": v(-6.18, -12.7) * mm, "end": v(-5.99, -12.99) * mm});
            skLineSegment(sketch, "E99.3.6", {"start": v(-3.44, -15.54) * mm, "end": v(-5.99, -12.99) * mm});
            skArc(sketch, "E99.3.7", {"start": v(-3.44, -15.54) * mm, "mid": v(-2.46, -15.73) * mm, "end": v(-1.9, -14.9) * mm});
            skLineSegment(sketch, "E99.3.8", {"start": v(-1.9, -12.4) * mm, "end": v(-1.9, -14.9) * mm});
            skLineSegment(sketch, "E99.3.9", {"start": v(-0.1, -12.4) * mm, "end": v(-1.9, -12.4) * mm});
            skLineSegment(sketch, "E99.3.10", {"start": v(-0.1, -7.6) * mm, "end": v(-0.1, -12.4) * mm});
            skLineSegment(sketch, "E99.3.11", {"start": v(-0.1, -7.6) * mm, "end": v(-1.9, -7.6) * mm});
            skPoint(sketch, "E99.center", {"position": v(-10, -10) * mm});
            skSolve(sketch);
        }
        {
            var Q0;
            Q0=makeQuery(id+"F15.imprint","IMPRINT",FACE,{"disambiguationData":[TD([[makeQuery(id+"F15.imprint","IMPRINT",EDGE,{"derivedFrom":sQuery(id+"F15.wireOp",EDGE,"E98.0")}),1.0]])]});
            var Q1;
            Q1=makeQuery(id+"F15.imprint","IMPRINT",FACE,{"disambiguationData":[TD([[makeQuery(id+"F15.imprint","IMPRINT",EDGE,{"derivedFrom":sQuery(id+"F15.wireOp",EDGE,"E99.1.0")}),-1.0]])]});
            var Q2;
            Q2=makeQuery(id+"F15.imprint","IMPRINT",FACE,{"disambiguationData":[TD([[makeQuery(id+"F15.imprint","IMPRINT",EDGE,{"derivedFrom":sQuery(id+"F15.wireOp",EDGE,"E99.3.0")}),-1.0]])]});
            var Q3;
            Q3=makeQuery(id+"F15.imprint","IMPRINT",FACE,{"disambiguationData":[TD([[makeQuery(id+"F15.imprint","IMPRINT",EDGE,{"derivedFrom":sQuery(id+"F15.wireOp",EDGE,"E99.2.0")}),-1.0]])]});
            extrude(context, id + "F16", {"entities" : qUnion([Q0, Q1, Q2, Q3]), "operationType" : NewBodyOperationType.ADD, "depth" : 5 * mm, "offsetDistance" : 25 * mm});
        }
        {
            var Q0;
            Q0=makeQuery(id+"F1.opExtrude","SWEPT_FACE",FACE,{"disambiguationData":[OSD([sQuery(id+"F0.wireOp",EDGE,"E0.left")])]});
            var sketch = newSketch(context, id + "F17", { "sketchPlane" : qUnion([Q0])});
            skLineSegment(sketch, "E100", {"start": v(0, 20) * mm, "end": v(0, 30) * mm});
            skLineSegment(sketch, "E101", {"start": v(20, 0) * mm, "end": v(30, 0) * mm});
            skLineSegment(sketch, "E102.0", {"start": v(9.7, 29.7) * mm, "end": v(29.7, 9.7) * mm});
            skPoint(sketch, "E103", {"position": v(19.7, 19.7) * mm});
            skLineSegment(sketch, "E104.0", {"start": v(0, 30) * mm, "end": v(9, 30) * mm});
            skPoint(sketch, "E105.orphan", {"position": v(2.2, 37.2) * mm});
            skPoint(sketch, "E106.endSnap0", {"position": v(13.75, 10) * mm});
            skLineSegment(sketch, "E107.0", {"start": v(30, 0) * mm, "end": v(30, 9) * mm});
            skPoint(sketch, "E108.orphan", {"position": v(37.2, 2.2) * mm});
            skLineSegment(sketch, "E109", {"start": v(0, 20) * mm, "end": v(19, 20) * mm});
            skLineSegment(sketch, "E110", {"start": v(20, 0) * mm, "end": v(20, 19) * mm});
            skArc(sketch, "E111", {"start": v(20, 19) * mm, "mid": v(19.7, 19.7) * mm, "end": v(19, 20) * mm});
            skPoint(sketch, "E112.visualSharp", {"position": v(30, 9.4) * mm});
            skArc(sketch, "E112.filletArc", {"start": v(30, 9) * mm, "mid": v(29.92, 9.38) * mm, "end": v(29.7, 9.7) * mm});
            skPoint(sketch, "E113.visualSharp", {"position": v(9.4, 30) * mm});
            skArc(sketch, "E113.filletArc", {"start": v(9.7, 29.7) * mm, "mid": v(9.38, 29.92) * mm, "end": v(9, 30) * mm});
            skSolve(sketch);
        }
        {
            var Q0;
            Q0=makeQuery(id+"F17.imprint","IMPRINT",FACE,{"disambiguationData":[TD([[makeQuery(id+"F17.imprint","IMPRINT",EDGE,{"derivedFrom":sQuery(id+"F17.wireOp",EDGE,"E101")}),1.0]])]});
            var Q1;
            Q1=makeQuery(id+"F17.imprint","IMPRINT",FACE,{"disambiguationData":[TD([[makeQuery(id+"F17.imprint","IMPRINT",EDGE,{"derivedFrom":sQuery(id+"F17.wireOp",EDGE,"E100")}),-1.0]])]});
            extrude(context, id + "F18", {"entities" : qUnion([Q0, Q1]), "operationType" : NewBodyOperationType.ADD, "oppositeDirection" : true, "depth" : 1.7 * mm, "offsetDistance" : 25 * mm});
        }
        {
            var Q0;
            Q0=makeQuery(id+"F18.boolean.opBoolean","MERGE",FACE,{"derivedFrom":[makeQuery(id+"F1.opExtrude","CAP_FACE",FACE,{"disambiguationData":[OSD([sQuery(id+"F0.wireOp",EDGE,"E0.bottom"),sQuery(id+"F0.wireOp",EDGE,"E0.top"),sQuery(id+"F0.wireOp",EDGE,"E0.left"),sQuery(id+"F0.wireOp",EDGE,"E0.right")])],"isStart":true}),makeQuery(id+"F18.opExtrude","SWEPT_FACE",FACE,{"disambiguationData":[OSD([sQuery(id+"F17.wireOp",EDGE,"E101")])]})]});
            var sketch = newSketch(context, id + "F19", { "sketchPlane" : qUnion([Q0]) });
            skLineSegment(sketch, "E114", {"start": v(-20, -19) * mm, "end": v(-20, 0) * mm});
            skLineSegment(sketch, "E115", {"start": v(-20, 0) * mm, "end": v(-30, 0) * mm});
            skLineSegment(sketch, "E116", {"start": v(-30, 0) * mm, "end": v(-30, -9) * mm});
            skLineSegment(sketch, "E117", {"start": v(-19, -20) * mm, "end": v(-1.7, -20) * mm});
            skLineSegment(sketch, "E118", {"start": v(-1.7, -30) * mm, "end": v(-9, -30) * mm});
            skArc(sketch, "E119", {"start": v(-20, -19) * mm, "mid": v(-19.7, -19.7) * mm, "end": v(-19, -20) * mm});
            skLineSegment(sketch, "E120", {"start": v(-1.7, -20) * mm, "end": v(-1.7, -30) * mm});
            skLineSegment(sketch, "E121.0", {"start": v(-29.7, -9.7) * mm, "end": v(-9.7, -29.7) * mm});
            skPoint(sketch, "E122", {"position": v(-19.7, -19.7) * mm});
            skPoint(sketch, "E123.visualSharp", {"position": v(-9.41, -30) * mm});
            skArc(sketch, "E123.filletArc", {"start": v(-9.7, -29.7) * mm, "mid": v(-9.38, -29.92) * mm, "end": v(-9, -30) * mm});
            skPoint(sketch, "E124.visualSharp", {"position": v(-30, -9.41) * mm});
            skArc(sketch, "E124.filletArc", {"start": v(-30, -9) * mm, "mid": v(-29.92, -9.38) * mm, "end": v(-29.7, -9.7) * mm});
            skSolve(sketch);
        }
        {
            var Q0;
            {var subQ1=sQuery(id+"F19.wireOp",EDGE,"E117");Q0=makeQuery(id+"F19.imprint","IMPRINT",FACE,{"disambiguationData":[TD([[makeQuery(id+"F19.imprint","IMPRINT",EDGE,{"derivedFrom":subQ1}),1.0]])]});}
            var Q1;
            {var subQ2=sQuery(id+"F19.wireOp",EDGE,"E114");Q1=makeQuery(id+"F19.imprint","IMPRINT",FACE,{"disambiguationData":[TD([[makeQuery(id+"F19.imprint","IMPRINT",EDGE,{"derivedFrom":subQ2}),-1.0]])]});}
            extrude(context, id + "F20", {"entities" : qUnion([Q0, Q1]), "operationType" : NewBodyOperationType.ADD, "oppositeDirection" : true, "depth" : 1.7 * mm, "offsetDistance" : 25 * mm});
        }
        {
            var Q0;
            Q0=makeQuery(id+"F20.boolean.opBoolean","MERGE",FACE,{"derivedFrom":[makeQuery(id+"F18.boolean.opBoolean","MERGE",FACE,{"derivedFrom":[makeQuery(id+"F1.opExtrude","SWEPT_FACE",FACE,{"disambiguationData":[OSD([sQuery(id+"F0.wireOp",EDGE,"E0.bottom")])]}),makeQuery(id+"F18.opExtrude","SWEPT_FACE",FACE,{"disambiguationData":[OSD([sQuery(id+"F17.wireOp",EDGE,"E100")])]})]}),makeQuery(id+"F20.opExtrude","SWEPT_FACE",FACE,{"disambiguationData":[OSD([sQuery(id+"F19.wireOp",EDGE,"E115")])]})]});
            var sketch = newSketch(context, id + "F21", { "sketchPlane" : qUnion([Q0]) });
            skLineSegment(sketch, "E125", {"start": v(-20, 19) * mm, "end": v(-20, 1.7) * mm});
            skLineSegment(sketch, "E126", {"start": v(-20, 1.7) * mm, "end": v(-30, 1.7) * mm});
            skLineSegment(sketch, "E127", {"start": v(-30, 1.7) * mm, "end": v(-30, 9) * mm});
            skLineSegment(sketch, "E128", {"start": v(-19, 20) * mm, "end": v(-1.7, 20) * mm});
            skLineSegment(sketch, "E129", {"start": v(-1.7, 20) * mm, "end": v(-1.7, 30) * mm});
            skLineSegment(sketch, "E130", {"start": v(-1.7, 30) * mm, "end": v(-9, 30) * mm});
            skLineSegment(sketch, "E131.0", {"start": v(-29.7, 9.7) * mm, "end": v(-19.7, 19.7) * mm});
            skPoint(sketch, "E132", {"position": v(-19.7, 19.7) * mm});
            skArc(sketch, "E133", {"start": v(-19, 20) * mm, "mid": v(-19.7, 19.7) * mm, "end": v(-20, 19) * mm});
            skPoint(sketch, "E134.visualSharp", {"position": v(-30, 9.41) * mm});
            skArc(sketch, "E134.filletArc", {"start": v(-29.7, 9.7) * mm, "mid": v(-29.92, 9.38) * mm, "end": v(-30, 9) * mm});
            skPoint(sketch, "E135.visualSharp", {"position": v(-9.41, 30) * mm});
            skArc(sketch, "E135.filletArc", {"start": v(-9, 30) * mm, "mid": v(-9.38, 29.92) * mm, "end": v(-9.7, 29.7) * mm});
            skLineSegment(sketch, "E136", {"start": v(-19.7, 19.7) * mm, "end": v(-9.7, 29.7) * mm});
            skSolve(sketch);
        }
        {
            var Q0;
            {var subQ4=sQuery(id+"F21.wireOp",EDGE,"E125");Q0=makeQuery(id+"F21.imprint","IMPRINT",FACE,{"disambiguationData":[TD([[makeQuery(id+"F21.imprint","IMPRINT",EDGE,{"derivedFrom":subQ4}),-1.0]])]});}
            var Q1;
            {var subQ4=sQuery(id+"F21.wireOp",EDGE,"E128");Q1=makeQuery(id+"F21.imprint","IMPRINT",FACE,{"disambiguationData":[TD([[makeQuery(id+"F21.imprint","IMPRINT",EDGE,{"derivedFrom":subQ4}),-1.0]])]});}
            extrude(context, id + "F22", {"entities" : qUnion([Q0, Q1]), "operationType" : NewBodyOperationType.ADD, "oppositeDirection" : true, "depth" : 1.7 * mm, "offsetDistance" : 25 * mm});
        }
        {
            var Q0;
            Q0=makeQuery(id+"F1.opExtrude","CAP_FACE",FACE,{"disambiguationData":[OSD([sQuery(id+"F0.wireOp",EDGE,"E0.bottom"),sQuery(id+"F0.wireOp",EDGE,"E0.top"),sQuery(id+"F0.wireOp",EDGE,"E0.left"),sQuery(id+"F0.wireOp",EDGE,"E0.right")])],"isStart":false});
            var sketch = newSketch(context, id + "F23", { "sketchPlane" : qUnion([Q0]) });
            skLineSegment(sketch, "E137", {"start": v(-1.7, 1.7) * mm, "end": v(-19, 19) * mm, "construction": true});
            skLineSegment(sketch, "E138", {"start": v(-19, 1.7) * mm, "end": v(-1.7, 19) * mm, "construction": true});
            skLineSegment(sketch, "E139.0", {"start": v(-10.38, 1.7) * mm, "end": v(-1.7, 10.38) * mm});
            skPoint(sketch, "E140", {"position": v(-6.04, 6.04) * mm});
            skLineSegment(sketch, "E141", {"start": v(-1.7, 1.7) * mm, "end": v(-10.38, 1.7) * mm});
            skLineSegment(sketch, "E142", {"start": v(-1.7, 1.7) * mm, "end": v(-1.7, 10.38) * mm});
            skPoint(sketch, "E143.orphan", {"position": v(2.6, 14.7) * mm});
            skPoint(sketch, "E144.orphan", {"position": v(-14.7, -2.6) * mm});
            skSolve(sketch);
        }
        {
            var Q0;
            {var subQ0=sQuery(id+"F23.wireOp",EDGE,"E141");Q0=makeQuery(id+"F23.imprint","IMPRINT",FACE,{"disambiguationData":[TD([[makeQuery(id+"F23.imprint","IMPRINT",EDGE,{"derivedFrom":subQ0}),-1.0]])]});}
            var Q1;
            Q1=makeQuery(id+"F22.boolean.opBoolean","MERGE",FACE,{"derivedFrom":[makeQuery(id+"F18.opExtrude","SWEPT_FACE",FACE,{"disambiguationData":[OSD([sQuery(id+"F17.wireOp",EDGE,"E104.0")])]}),makeQuery(id+"F22.opExtrude","SWEPT_FACE",FACE,{"disambiguationData":[OSD([sQuery(id+"F21.wireOp",EDGE,"E130")])]})]});
            var Q2;
            Q2=makeQuery(id+"F1.opExtrude","SWEPT_BODY",BODY,{"disambiguationData":[OSD([sQuery(id+"F0.wireOp",EDGE,"E0.bottom"),sQuery(id+"F0.wireOp",EDGE,"E0.top"),sQuery(id+"F0.wireOp",EDGE,"E0.left"),sQuery(id+"F0.wireOp",EDGE,"E0.right")])]});
            extrude(context, id + "F24", {"entities" : qUnion([Q0]), "operationType" : NewBodyOperationType.ADD, "endBound" : BoundingType.UP_TO_SURFACE, "depth" : 25 * mm, "endBoundEntityFace" : qUnion([Q1]), "endBoundEntityBody" : qUnion([Q2]), "offsetDistance" : 25 * mm});
        }
        {
            var Q0;
            Q0=makeQuery(id+"F24.opExtrude","SWEPT_FACE",FACE,{"disambiguationData":[OSD([sQuery(id+"F23.wireOp",EDGE,"E141")])]});
            extrude(context, id + "F25", {"entities" : qUnion([Q0]), "operationType" : NewBodyOperationType.REMOVE, "endBound" : BoundingType.THROUGH_ALL, "oppositeDirection" : true, "depth" : 25 * mm, "offsetDistance" : 25 * mm});
        }
        {
            var Q0;
            Q0=makeQuery(id+"F24.opExtrude","SWEPT_FACE",FACE,{"disambiguationData":[OSD([sQuery(id+"F23.wireOp",EDGE,"E142")])]});
            extrude(context, id + "F26", {"entities" : qUnion([Q0]), "operationType" : NewBodyOperationType.REMOVE, "endBound" : BoundingType.THROUGH_ALL, "oppositeDirection" : true, "depth" : 25 * mm, "offsetDistance" : 25 * mm});
        }
        {
            var Q0;
            Q0=makeQuery(id+"F24.opExtrude","SWEPT_FACE",FACE,{"disambiguationData":[OSD([sQuery(id+"F23.wireOp",EDGE,"E139.0")])]});
            var sketch = newSketch(context, id + "F27", { "sketchPlane" : qUnion([Q0]) });
            skCircle(sketch, "E145", {"center": v(0, 25) * mm, "radius": 2.55 * mm});
            skSolve(sketch);
        }
        {
            var Q0;
            Q0=makeQuery(id+"F27.imprint","IMPRINT",FACE,{"disambiguationData":[TD([[makeQuery(id+"F27.imprint","IMPRINT",EDGE,{"derivedFrom":sQuery(id+"F27.wireOp",EDGE,"E145")}),1.0]])]});
            extrude(context, id + "F28", {"entities" : qUnion([Q0]), "operationType" : NewBodyOperationType.REMOVE, "endBound" : BoundingType.THROUGH_ALL, "oppositeDirection" : true, "depth" : 25 * mm, "offsetDistance" : 25 * mm});
        }
        {
            var Q0;
            Q0=makeQuery(id+"F1.opExtrude","SWEPT_FACE",FACE,{"disambiguationData":[OSD([sQuery(id+"F0.wireOp",EDGE,"E0.top")])]});
            var sketch = newSketch(context, id + "F29", { "sketchPlane" : qUnion([Q0]) });
            skLineSegment(sketch, "E146.0", {"start": v(1.7, 10.38) * mm, "end": v(10.38, 1.7) * mm});
            skLineSegment(sketch, "E147", {"start": v(1.7, 1.7) * mm, "end": v(1.7, 10.38) * mm});
            skLineSegment(sketch, "E148", {"start": v(1.7, 1.7) * mm, "end": v(10.38, 1.7) * mm});
            skSolve(sketch);
        }
        {
            var Q0;
            {var subQ0=sQuery(id+"F29.wireOp",EDGE,"E147");Q0=makeQuery(id+"F29.imprint","IMPRINT",FACE,{"disambiguationData":[TD([[makeQuery(id+"F29.imprint","IMPRINT",EDGE,{"derivedFrom":subQ0}),1.0]])]});}
            var Q1;
            Q1=makeQuery(id+"F20.boolean.opBoolean","MERGE",FACE,{"derivedFrom":[makeQuery(id+"F18.opExtrude","SWEPT_FACE",FACE,{"disambiguationData":[OSD([sQuery(id+"F17.wireOp",EDGE,"E107.0")])]}),makeQuery(id+"F20.opExtrude","SWEPT_FACE",FACE,{"disambiguationData":[OSD([sQuery(id+"F19.wireOp",EDGE,"E118")])]})]});
            extrude(context, id + "F30", {"entities" : qUnion([Q0]), "operationType" : NewBodyOperationType.ADD, "endBound" : BoundingType.UP_TO_SURFACE, "depth" : 25 * mm, "endBoundEntityFace" : qUnion([Q1]), "offsetDistance" : 25 * mm});
        }
        {
            var Q0;
            Q0=makeQuery(id+"F30.opExtrude","SWEPT_FACE",FACE,{"disambiguationData":[OSD([sQuery(id+"F29.wireOp",EDGE,"E147")])]});
            extrude(context, id + "F31", {"entities" : qUnion([Q0]), "operationType" : NewBodyOperationType.REMOVE, "endBound" : BoundingType.THROUGH_ALL, "oppositeDirection" : true, "depth" : 25 * mm, "offsetDistance" : 25 * mm});
        }
        {
            var Q0;
            Q0=makeQuery(id+"F30.opExtrude","SWEPT_FACE",FACE,{"disambiguationData":[OSD([sQuery(id+"F29.wireOp",EDGE,"E148")])]});
            extrude(context, id + "F32", {"entities" : qUnion([Q0]), "operationType" : NewBodyOperationType.REMOVE, "endBound" : BoundingType.THROUGH_ALL, "oppositeDirection" : true, "depth" : 25 * mm, "offsetDistance" : 25 * mm});
        }
        {
            var Q0;
            Q0=makeQuery(id+"F30.opExtrude","SWEPT_FACE",FACE,{"disambiguationData":[OSD([sQuery(id+"F29.wireOp",EDGE,"E146.0")])]});
            var sketch = newSketch(context, id + "F33", { "sketchPlane" : qUnion([Q0]) });
            skCircle(sketch, "E149", {"center": v(0, 25) * mm, "radius": 2.55 * mm});
            skSolve(sketch);
        }
        {
            var Q0;
            Q0=makeQuery(id+"F33.imprint","IMPRINT",FACE,{"disambiguationData":[TD([[makeQuery(id+"F33.imprint","IMPRINT",EDGE,{"derivedFrom":sQuery(id+"F33.wireOp",EDGE,"E149")}),1.0]])]});
            extrude(context, id + "F34", {"entities" : qUnion([Q0]), "operationType" : NewBodyOperationType.REMOVE, "endBound" : BoundingType.THROUGH_ALL, "oppositeDirection" : true, "depth" : 25 * mm, "offsetDistance" : 25 * mm});
        }
        {
            var Q0;
            Q0=makeQuery(id+"F1.opExtrude","SWEPT_FACE",FACE,{"disambiguationData":[OSD([sQuery(id+"F0.wireOp",EDGE,"E0.right")])]});
            var sketch = newSketch(context, id + "F35", { "sketchPlane" : qUnion([Q0]) });
            skLineSegment(sketch, "E150", {"start": v(-1.7, 10.38) * mm, "end": v(-10.38, 1.7) * mm});
            skLineSegment(sketch, "E151", {"start": v(-1.7, 1.7) * mm, "end": v(-10.38, 1.7) * mm});
            skLineSegment(sketch, "E152", {"start": v(-1.7, 1.7) * mm, "end": v(-1.7, 10.38) * mm});
            skSolve(sketch);
        }
        {
            var Q0;
            {var subQ3=sQuery(id+"F35.wireOp",EDGE,"E151");Q0=makeQuery(id+"F35.imprint","IMPRINT",FACE,{"disambiguationData":[TD([[makeQuery(id+"F35.imprint","IMPRINT",EDGE,{"derivedFrom":subQ3}),-1.0]])]});}
            var Q1;
            Q1=makeQuery(id+"F22.boolean.opBoolean","MERGE",FACE,{"derivedFrom":[makeQuery(id+"F20.opExtrude","SWEPT_FACE",FACE,{"disambiguationData":[OSD([sQuery(id+"F19.wireOp",EDGE,"E116")])]}),makeQuery(id+"F22.opExtrude","SWEPT_FACE",FACE,{"disambiguationData":[OSD([sQuery(id+"F21.wireOp",EDGE,"E127")])]})]});
            extrude(context, id + "F36", {"entities" : qUnion([Q0]), "operationType" : NewBodyOperationType.ADD, "endBound" : BoundingType.UP_TO_SURFACE, "depth" : 25 * mm, "endBoundEntityFace" : qUnion([Q1]), "offsetDistance" : 25 * mm});
        }
        {
            var Q0;
            Q0=makeQuery(id+"F36.opExtrude","SWEPT_FACE",FACE,{"disambiguationData":[OSD([sQuery(id+"F35.wireOp",EDGE,"E150")])]});
            var sketch = newSketch(context, id + "F37", { "sketchPlane" : qUnion([Q0]) });
            skCircle(sketch, "E153", {"center": v(25, 0) * mm, "radius": 2.55 * mm});
            skSolve(sketch);
        }
        {
            var Q0;
            Q0=makeQuery(id+"F37.imprint","IMPRINT",FACE,{"disambiguationData":[TD([[makeQuery(id+"F37.imprint","IMPRINT",EDGE,{"derivedFrom":sQuery(id+"F37.wireOp",EDGE,"E153")}),1.0]])]});
            extrude(context, id + "F38", {"entities" : qUnion([Q0]), "operationType" : NewBodyOperationType.REMOVE, "endBound" : BoundingType.THROUGH_ALL, "oppositeDirection" : true, "depth" : 25 * mm, "offsetDistance" : 25 * mm});
        }
        {
            var Q0;
            Q0=makeQuery(id+"F36.opExtrude","SWEPT_FACE",FACE,{"disambiguationData":[OSD([sQuery(id+"F35.wireOp",EDGE,"E152")])]});
            extrude(context, id + "F39", {"entities" : qUnion([Q0]), "operationType" : NewBodyOperationType.REMOVE, "endBound" : BoundingType.THROUGH_ALL, "oppositeDirection" : true, "depth" : 25 * mm, "offsetDistance" : 25 * mm});
        }
        {
            var Q0;
            Q0=makeQuery(id+"F36.opExtrude","SWEPT_FACE",FACE,{"disambiguationData":[OSD([sQuery(id+"F35.wireOp",EDGE,"E151")])]});
            extrude(context, id + "F40", {"entities" : qUnion([Q0]), "operationType" : NewBodyOperationType.REMOVE, "endBound" : BoundingType.THROUGH_ALL, "oppositeDirection" : true, "depth" : 25 * mm, "offsetDistance" : 25 * mm});
        }
        {
            var Q0;
            {var subQ0=sQuery(id+"F21.wireOp",EDGE,"E128");var subQ1=sQuery(id+"F23.wireOp",EDGE,"E139.0");Q0=makeQuery(id+"F24.boolean.opBoolean","SPLIT",EDGE,{"disambiguationData":[topologyDisambiguationEdgeConnected([makeQuery(id+"F22.opExtrude","CAP_FACE",FACE,{"disambiguationData":[OSD([subQ0,sQuery(id+"F21.wireOp",EDGE,"E129"),sQuery(id+"F21.wireOp",EDGE,"E130"),sQuery(id+"F21.wireOp",EDGE,"E131.0"),sQuery(id+"F21.wireOp",EDGE,"E133"),sQuery(id+"F21.wireOp",EDGE,"E135.filletArc")])],"isStart":false})])],"derivedFrom":makeQuery(id+"F24.opExtrude","SWEPT_EDGE",EDGE,{"disambiguationData":[OSD([subQ0,subQ1,sQuery(id+"F23.wireOp",EDGE,"E141")])]})});}
            var Q1;
            {var subQ0=sQuery(id+"F17.wireOp",EDGE,"E109");var subQ1=sQuery(id+"F0.wireOp",EDGE,"E0.left");var subQ2=sQuery(id+"F23.wireOp",EDGE,"E139.0");Q1=makeQuery(id+"F24.boolean.opBoolean","SPLIT",EDGE,{"disambiguationData":[topologyDisambiguationEdgeConnected([makeQuery(id+"F18.opExtrude","CAP_FACE",FACE,{"disambiguationData":[OSD([sQuery(id+"F0.wireOp",EDGE,"E0.top"),subQ1,sQuery(id+"F17.wireOp",EDGE,"E100"),sQuery(id+"F17.wireOp",EDGE,"E102.0"),sQuery(id+"F17.wireOp",EDGE,"E104.0"),subQ0,sQuery(id+"F17.wireOp",EDGE,"E113.filletArc")])],"isStart":false})])],"derivedFrom":makeQuery(id+"F24.opExtrude","SWEPT_EDGE",EDGE,{"disambiguationData":[OSD([subQ1,subQ0,subQ2,sQuery(id+"F23.wireOp",EDGE,"E142")])]})});}
            var Q2;
            {var subQ0=sQuery(id+"F0.wireOp",EDGE,"E0.left");var subQ1=sQuery(id+"F0.wireOp",EDGE,"E0.top");var subQ4=sQuery(id+"F23.wireOp",EDGE,"E139.0");Q2=makeQuery(id+"F24.boolean.opBoolean","SPLIT",EDGE,{"disambiguationData":[TD([makeQuery(id+"F18.opExtrude","CAP_FACE",FACE,{"disambiguationData":[OSD([subQ1,subQ0,sQuery(id+"F17.wireOp",EDGE,"E100"),sQuery(id+"F17.wireOp",EDGE,"E102.0"),sQuery(id+"F17.wireOp",EDGE,"E104.0"),sQuery(id+"F17.wireOp",EDGE,"E109"),sQuery(id+"F17.wireOp",EDGE,"E113.filletArc")])],"isStart":false})])],"derivedFrom":makeQuery(id+"F24.opExtrude","CAP_EDGE",EDGE,{"disambiguationData":[OSD([subQ4])],"isStart":true})});}
            var Q3;
            {var subQ0=sQuery(id+"F21.wireOp",EDGE,"E125");var subQ1=sQuery(id+"F35.wireOp",EDGE,"E150");Q3=makeQuery(id+"F36.boolean.opBoolean","SPLIT",EDGE,{"disambiguationData":[topologyDisambiguationEdgeConnected([makeQuery(id+"F22.opExtrude","CAP_FACE",FACE,{"disambiguationData":[OSD([subQ0,sQuery(id+"F21.wireOp",EDGE,"E126"),sQuery(id+"F21.wireOp",EDGE,"E127"),sQuery(id+"F21.wireOp",EDGE,"E131.0"),sQuery(id+"F21.wireOp",EDGE,"E133"),sQuery(id+"F21.wireOp",EDGE,"E134.filletArc")])],"isStart":false})])],"derivedFrom":makeQuery(id+"F36.opExtrude","SWEPT_EDGE",EDGE,{"disambiguationData":[OSD([subQ0,subQ1,sQuery(id+"F35.wireOp",EDGE,"E152")])]})});}
            var Q4;
            {var subQ0=sQuery(id+"F35.wireOp",EDGE,"E150");Q4=makeQuery(id+"F36.boolean.opBoolean","SPLIT",EDGE,{"disambiguationData":[TD([makeQuery(id+"F22.opExtrude","CAP_FACE",FACE,{"disambiguationData":[OSD([sQuery(id+"F21.wireOp",EDGE,"E125"),sQuery(id+"F21.wireOp",EDGE,"E126"),sQuery(id+"F21.wireOp",EDGE,"E127"),sQuery(id+"F21.wireOp",EDGE,"E131.0"),sQuery(id+"F21.wireOp",EDGE,"E133"),sQuery(id+"F21.wireOp",EDGE,"E134.filletArc")])],"isStart":false})])],"derivedFrom":makeQuery(id+"F36.opExtrude","CAP_EDGE",EDGE,{"disambiguationData":[OSD([subQ0])],"isStart":true})});}
            var Q5;
            {var subQ0=sQuery(id+"F19.wireOp",EDGE,"E114");var subQ1=sQuery(id+"F35.wireOp",EDGE,"E150");Q5=makeQuery(id+"F36.boolean.opBoolean","SPLIT",EDGE,{"disambiguationData":[topologyDisambiguationEdgeConnected([makeQuery(id+"F20.opExtrude","CAP_FACE",FACE,{"disambiguationData":[OSD([subQ0,sQuery(id+"F19.wireOp",EDGE,"E115"),sQuery(id+"F19.wireOp",EDGE,"E116"),sQuery(id+"F19.wireOp",EDGE,"E119"),sQuery(id+"F19.wireOp",EDGE,"E121.0"),sQuery(id+"F19.wireOp",EDGE,"E124.filletArc")])],"isStart":false})])],"derivedFrom":makeQuery(id+"F36.opExtrude","SWEPT_EDGE",EDGE,{"disambiguationData":[OSD([subQ0,subQ1,sQuery(id+"F35.wireOp",EDGE,"E151")])]})});}
            var Q6;
            {var subQ0=sQuery(id+"F17.wireOp",EDGE,"E110");var subQ1=sQuery(id+"F29.wireOp",EDGE,"E146.0");Q6=makeQuery(id+"F30.boolean.opBoolean","SPLIT",EDGE,{"disambiguationData":[topologyDisambiguationEdgeConnected([makeQuery(id+"F18.opExtrude","CAP_FACE",FACE,{"disambiguationData":[OSD([sQuery(id+"F0.wireOp",EDGE,"E0.top"),sQuery(id+"F0.wireOp",EDGE,"E0.left"),sQuery(id+"F17.wireOp",EDGE,"E101"),sQuery(id+"F17.wireOp",EDGE,"E102.0"),sQuery(id+"F17.wireOp",EDGE,"E107.0"),subQ0,sQuery(id+"F17.wireOp",EDGE,"E112.filletArc")])],"isStart":false})])],"derivedFrom":makeQuery(id+"F30.opExtrude","SWEPT_EDGE",EDGE,{"disambiguationData":[OSD([subQ0,subQ1,sQuery(id+"F29.wireOp",EDGE,"E147")])]})});}
            var Q7;
            {var subQ0=sQuery(id+"F0.wireOp",EDGE,"E0.top");var subQ5=sQuery(id+"F0.wireOp",EDGE,"E0.left");var subQ7=sQuery(id+"F29.wireOp",EDGE,"E146.0");Q7=makeQuery(id+"F30.boolean.opBoolean","SPLIT",EDGE,{"disambiguationData":[TD([makeQuery(id+"F18.opExtrude","CAP_FACE",FACE,{"disambiguationData":[OSD([subQ0,subQ5,sQuery(id+"F17.wireOp",EDGE,"E101"),sQuery(id+"F17.wireOp",EDGE,"E102.0"),sQuery(id+"F17.wireOp",EDGE,"E107.0"),sQuery(id+"F17.wireOp",EDGE,"E110"),sQuery(id+"F17.wireOp",EDGE,"E112.filletArc")])],"isStart":false})])],"derivedFrom":makeQuery(id+"F30.opExtrude","CAP_EDGE",EDGE,{"disambiguationData":[OSD([subQ7])],"isStart":true})});}
            var Q8;
            {var subQ0=sQuery(id+"F19.wireOp",EDGE,"E117");var subQ1=sQuery(id+"F29.wireOp",EDGE,"E146.0");Q8=makeQuery(id+"F30.boolean.opBoolean","SPLIT",EDGE,{"disambiguationData":[topologyDisambiguationEdgeConnected([makeQuery(id+"F20.opExtrude","CAP_FACE",FACE,{"disambiguationData":[OSD([subQ0,sQuery(id+"F19.wireOp",EDGE,"E118"),sQuery(id+"F19.wireOp",EDGE,"E119"),sQuery(id+"F19.wireOp",EDGE,"E120"),sQuery(id+"F19.wireOp",EDGE,"E121.0"),sQuery(id+"F19.wireOp",EDGE,"E123.filletArc")])],"isStart":false})])],"derivedFrom":makeQuery(id+"F30.opExtrude","SWEPT_EDGE",EDGE,{"disambiguationData":[OSD([subQ0,subQ1,sQuery(id+"F29.wireOp",EDGE,"E148")])]})});}
            fillet(context, id + "F41", {"entities" : qUnion([Q0, Q1, Q2, Q3, Q4, Q5, Q6, Q7, Q8]), "radius" : 1.5 * mm, "tangentPropagation" : true});
        }
    });
